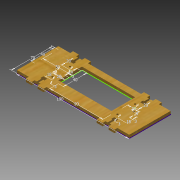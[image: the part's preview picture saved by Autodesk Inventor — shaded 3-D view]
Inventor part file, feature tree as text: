
AUTODESK INVENTOR PART (.ipt)
format: ipt  version: 2014 (Build 180170000, 170)  size: 285,184 bytes
history: native  units: mm
features: extrude x12, sketch x3
ambient origin geometry x8: Origin, YZ Plane, XZ Plane, XY Plane, X Axis, Y Axis, Z Axis, Center Point
bodies: Body1 (feature_tree)
feature tree (15):
  extrude  "Extrusion3"  Depth=70.0mm
  sketch  "Sketch3"  dims[d0=190.0mm d1=70.0mm]
  extrude  "Extrusion4"  Depth=5.0mm
  extrude  "Extrusion5"  Depth=3.5mm
  extrude  "Extrusion9"  Depth=3.5mm
  extrude  "Extrusion10"  Depth=5.0mm
  extrude  "Extrusion11"  Depth=2.0mm
  extrude  "Extrusion12"  Depth=2.0mm
  extrude  "Extrusion17"  Depth=40.0mm
  extrude  "Extrusion18"  Depth=8.0mm
  extrude  "Extrusion19"  Depth=13.0mm
  extrude  "Extrusion20"  Depth=40.0mm
  extrude  "Extrusion22"  Depth=13.0mm
  sketch  "Sketch4"  dims[d12=5.0mm d13=0.0mm d14=35.0mm]
  sketch  "Sketch5"  dims[d15=13.0mm d16=3.5mm d17=3.5mm d18=5.0mm d19=2.0mm d20=2.0mm d21=40.0mm d22=13.0mm d23=3.5mm d24=3.5mm d25=5.0mm d26=2.0mm d27=2.0mm d28=40.0mm d29=8.0mm d30=13.0mm d31=40.0mm d32=13.0mm d33=3.5mm d34=5.0mm d35=2.0mm d36=3.5mm d37=5.0mm d38=2.0mm d39=40.0mm d40=13.0mm d41=3.5mm d42=5.0mm d43=2.0mm d44=3.5mm d45=5.0mm d46=2.0mm d47=5.0mm d48=0.0mm d49=5.0mm d50=0.0mm d57=5.0mm d58=0.0mm d59=5.0mm d60=0.0mm d63=8.0mm d66=1.5mm d67=5.0mm d68=1.5mm d69=2.0mm d70=5.0mm d71=1.5mm d72=2.0mm d73=8.0mm d74=2.0mm d75=1.5mm d76=5.0mm d77=0.0mm d78=5.0mm d79=0.0mm d88=5.0mm d89=0.0mm d90=20.0mm d91=5.0mm d92=10.0mm d93=10.0mm d94=10.0mm d95=190.0mm d96=20.0mm d97=10.0mm d98=10.0mm d99=10.0mm d100=5.0mm d101=0.0mm d102=20.0mm d103=5.0mm d104=10.0mm d105=10.0mm d106=10.0mm d107=190.0mm d108=20.0mm d109=5.0mm d110=10.0mm d111=10.0mm d112=5.0mm d113=10.0mm d114=5.0mm d115=0.0mm d116=40.0mm d118=50.0mm d119=40.0mm d120=90.0mm d121=10.0mm d122=0.0mm d125=3.0mm d126=3.0mm d127=3.0mm d128=3.0mm d130=20.0mm d131=20.0mm d132=20.0mm d133=3.0mm d134=3.0mm d137=10.0mm d138=0.0mm d140=20.0mm d141=20.0mm d145=18.0mm d146=18.0mm]
